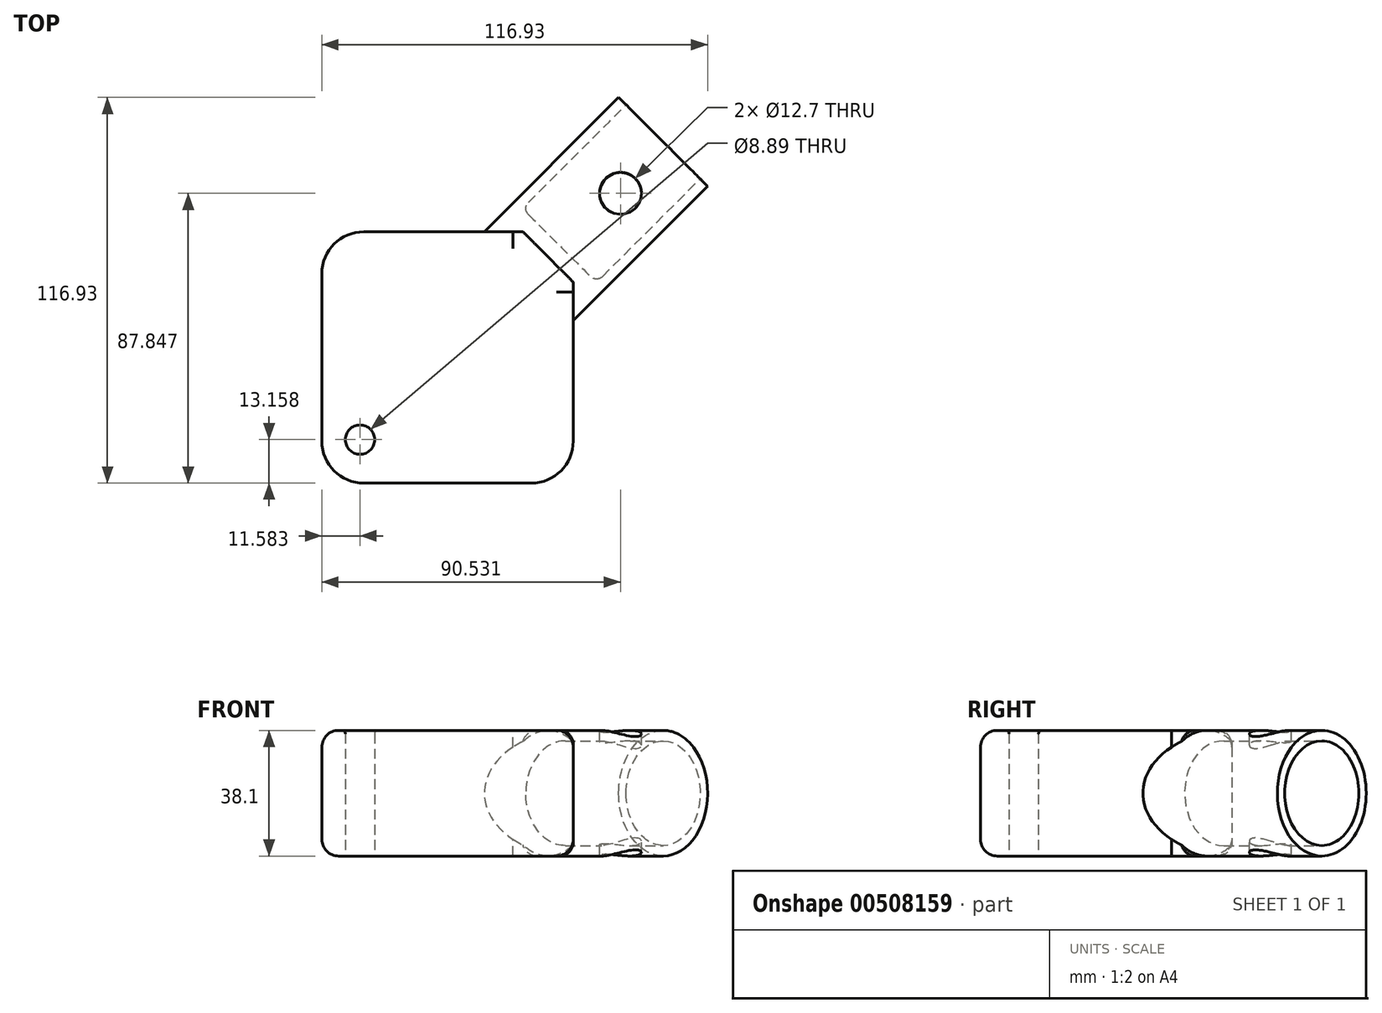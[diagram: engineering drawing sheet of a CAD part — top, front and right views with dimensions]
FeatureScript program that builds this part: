
annotation { "Feature Type Name" : "Feature", "Feature Type Description" : "" }
export const myFeature = defineFeature(function(context is Context, id is Id, definition is map)
    precondition{}
    {
        {
            var Q0;
            Q0=qCreatedBy(makeId("Top.planeOp"),FACE);
            var sketch = newSketch(context, id + "F0", { "sketchPlane" : qUnion([Q0])});
            skLineSegment(sketch, "E0.bottom", {"start": v(38.1, 38.1) * mm, "end": v(-38.1, 38.1) * mm});
            skLineSegment(sketch, "E0.top", {"start": v(38.1, -38.1) * mm, "end": v(-38.1, -38.1) * mm});
            skLineSegment(sketch, "E0.left", {"start": v(38.1, 38.1) * mm, "end": v(38.1, -38.1) * mm});
            skLineSegment(sketch, "E0.right", {"start": v(-38.1, 38.1) * mm, "end": v(-38.1, -38.1) * mm});
            skPoint(sketch, "E0.middle", {"position": v(0, 0) * mm});
            skCircle(sketch, "E1", {"center": v(-26.52, -24.94) * mm, "radius": 4.45 * mm});
            skSolve(sketch);
        }
        {
            var Q0;
            Q0 = qSketchRegion(id + "F0", true);
            extrude(context, id + "F1", {"entities" : qUnion([Q0]), "depth" : 38.1 * mm});
        }
        {
            var Q0;
            Q0=makeQuery(id+"F1.opExtrude","SWEPT_EDGE",EDGE,{"disambiguationData":[OSD([sQuery(id+"F0.wireOp",EDGE,"E0.bottom"),sQuery(id+"F0.wireOp",EDGE,"E0.right")])]});
            var Q1;
            Q1=makeQuery(id+"F1.opExtrude","SWEPT_EDGE",EDGE,{"disambiguationData":[OSD([sQuery(id+"F0.wireOp",EDGE,"E0.top"),sQuery(id+"F0.wireOp",EDGE,"E0.left")])]});
            var Q2;
            Q2=makeQuery(id+"F1.opExtrude","SWEPT_EDGE",EDGE,{"disambiguationData":[OSD([sQuery(id+"F0.wireOp",EDGE,"E0.top"),sQuery(id+"F0.wireOp",EDGE,"E0.right")])]});
            fillet(context, id + "F2", {"entities" : qUnion([Q0, Q1, Q2]), "radius" : 12.7 * mm, "tangentPropagation" : true, "allowEdgeOverflow" : false});
        }
        {
            var Q0;
            Q0=makeQuery(id+"F1.opExtrude","SWEPT_EDGE",EDGE,{"disambiguationData":[OSD([sQuery(id+"F0.wireOp",EDGE,"E0.bottom"),sQuery(id+"F0.wireOp",EDGE,"E0.left")])]});
            chamfer(context, id + "F3", {"entities" : qUnion([Q0]), "width" : 15.24 * mm, "tangentPropagation" : true});
        }
        {
            var Q0;
            Q0=makeQuery(id+"F3.opChamfer","BLEND_FACE",FACE,{"disambiguationData":[OSD([sQuery(id+"F0.wireOp",EDGE,"E0.bottom"),sQuery(id+"F0.wireOp",EDGE,"E0.left")])]});
            var sketch = newSketch(context, id + "F4", { "sketchPlane" : qUnion([Q0]), "disableImprinting" : false});
            skEllipse(sketch, "E2", {"center": v(0, 19.05) * mm, "majorRadius": 19.05 * mm, "minorRadius": 19.05 * mm, "majorAxis": v(1, 0)});
            skPoint(sketch, "E2.centerSnap0", {"position": v(10.78, 19.05) * mm});
            skSolve(sketch);
        }
        {
            var Q0;
            Q0 = qSketchRegion(id + "F4", true);
            extrude(context, id + "F5", {"entities" : qUnion([Q0]), "operationType" : NewBodyOperationType.ADD, "depth" : 98.67 * mm, "symmetric" : true});
        }
        {
            var Q0;
            Q0=makeQuery(id+"F1.opExtrude","CAP_EDGE",EDGE,{"disambiguationData":[OSD([sQuery(id+"F0.wireOp",EDGE,"E0.top")])],"isStart":false});
            var Q1;
            Q1=makeQuery(id+"F1.opExtrude","CAP_EDGE",EDGE,{"disambiguationData":[OSD([sQuery(id+"F0.wireOp",EDGE,"E0.top")])],"isStart":true});
            fillet(context, id + "F6", {"entities" : qUnion([Q0, Q1]), "radius" : 5.08 * mm, "tangentPropagation" : true, "allowEdgeOverflow" : false});
        }
        {
            var Q0;
            Q0=makeQuery(id+"F5.opExtrude","CAP_FACE",FACE,{"disambiguationData":[OSD([sQuery(id+"F4.wireOp",EDGE,"E2")])],"isStart":false});
            var sketch = newSketch(context, id + "F7", { "sketchPlane" : qUnion([Q0])});
            skCircle(sketch, "E3", {"center": v(0, 19.05) * mm, "radius": 15.88 * mm});
            skSolve(sketch);
        }
        {
            var Q0;
            Q0 = qSketchRegion(id + "F7", true);
            extrude(context, id + "F8", {"entities" : qUnion([Q0]), "operationType" : NewBodyOperationType.REMOVE, "oppositeDirection" : true, "depth" : 44.45 * mm});
        }
        {
            var Q0;
            Q0=qCreatedBy(makeId("Top.planeOp"),FACE);
            var sketch = newSketch(context, id + "F9", { "sketchPlane" : qUnion([Q0])});
            skCircle(sketch, "E4", {"center": v(52.43, 49.75) * mm, "radius": 6.35 * mm});
            skSolve(sketch);
        }
        {
            var Q0;
            Q0=makeQuery(id+"F9.imprint","IMPRINT",FACE,{"disambiguationData":[TD([[makeQuery(id+"F9.imprint","IMPRINT",EDGE,{"derivedFrom":sQuery(id+"F9.wireOp",EDGE,"E4")}),1.0]])]});
            extrude(context, id + "F10", {"entities" : qUnion([Q0]), "operationType" : NewBodyOperationType.REMOVE, "oppositeDirection" : true, "depth" : 122.82 * mm, "symmetric" : true});
        }
        {
            var Q0;
            Q0=makeQuery(id+"F8.boolean.opBoolean","COPY",EDGE,{"derivedFrom":makeQuery(id+"F8.opExtrude","CAP_EDGE",EDGE,{"disambiguationData":[OSD([sQuery(id+"F7.wireOp",EDGE,"E3")])],"isStart":false})});
            var Q1;
            Q1=makeQuery(id+"F8.boolean.opBoolean","COPY",EDGE,{"derivedFrom":makeQuery(id+"F8.opExtrude","CAP_EDGE",EDGE,{"disambiguationData":[OSD([sQuery(id+"F7.wireOp",EDGE,"E3")])],"isStart":true})});
            fillet(context, id + "F11", {"entities" : qUnion([Q0, Q1]), "radius" : 2.54 * mm, "tangentPropagation" : true, "allowEdgeOverflow" : false});
        }
        {
            var Q0;
            Q0=makeQuery(id+"F1.opExtrude","CAP_EDGE",EDGE,{"disambiguationData":[OSD([sQuery(id+"F0.wireOp",EDGE,"E1")])],"isStart":false});
            fillet(context, id + "F12", {"entities" : qUnion([Q0]), "radius" : 1.02 * mm, "tangentPropagation" : true, "allowEdgeOverflow" : false});
        }
    });
